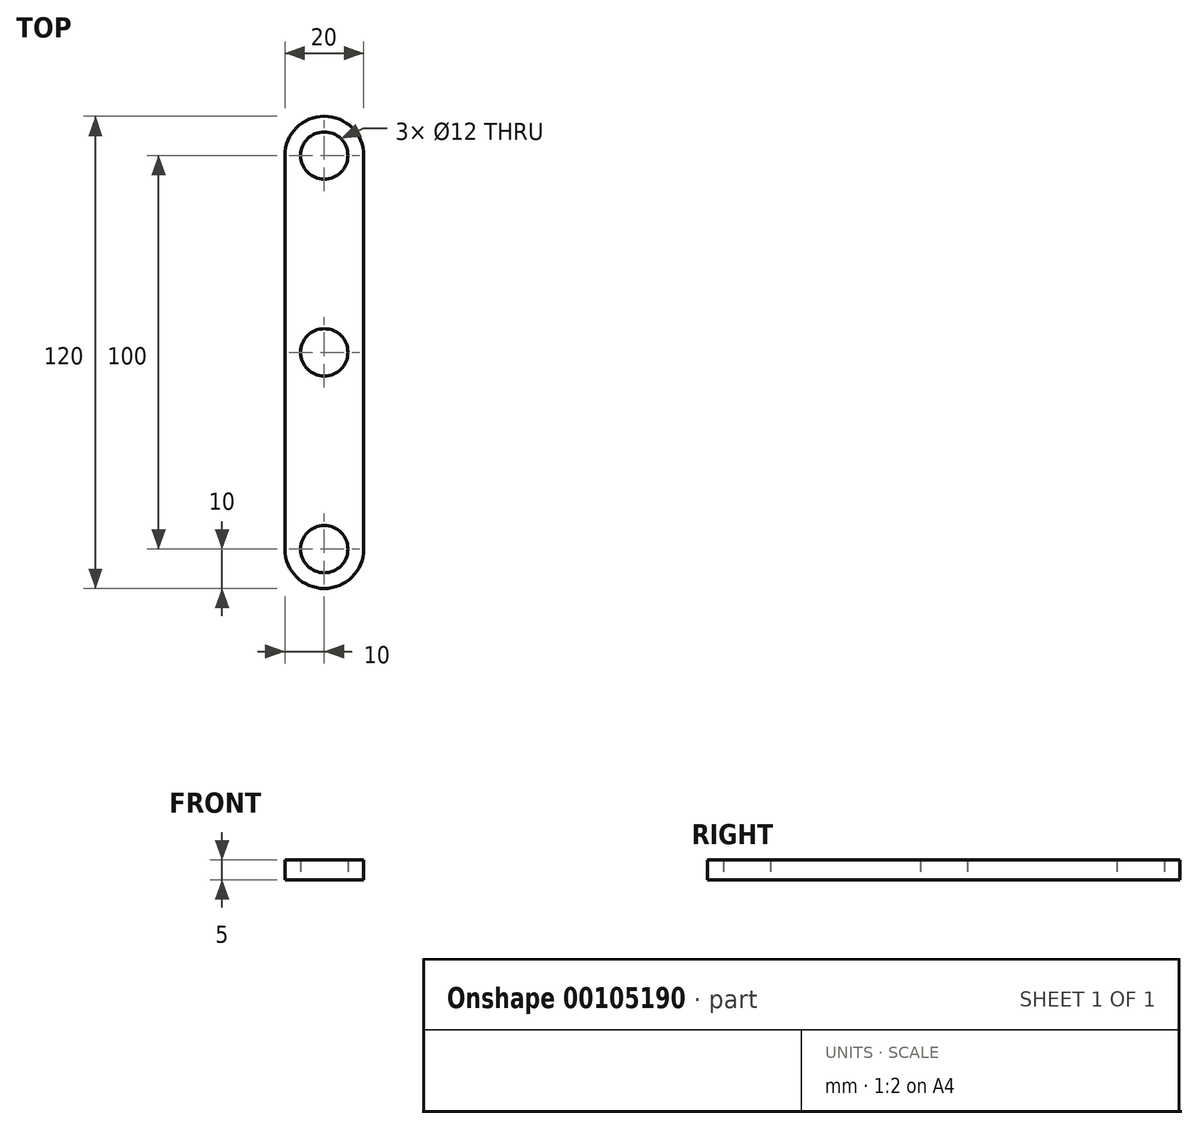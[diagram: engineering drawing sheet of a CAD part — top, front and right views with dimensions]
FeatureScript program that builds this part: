
annotation { "Feature Type Name" : "Feature", "Feature Type Description" : "" }
export const myFeature = defineFeature(function(context is Context, id is Id, definition is map)
    precondition{}
    {
        {
            var Q0;
            Q0=qCreatedBy(makeId("Top.planeOp"),FACE);
            var sketch = newSketch(context, id + "F0", { "sketchPlane" : qUnion([Q0])});
            skCircle(sketch, "E0", {"center": v(0, 0) * mm, "radius": 6 * mm});
            skCircle(sketch, "E1", {"center": v(0, 50) * mm, "radius": 6 * mm});
            skArc(sketch, "E2.0", {"start": v(-10, 0) * mm, "mid": v(0, -10) * mm, "end": v(10, 0) * mm});
            skArc(sketch, "E3", {"start": v(10, 100) * mm, "mid": v(0, 110) * mm, "end": v(-10, 100) * mm});
            skCircle(sketch, "E4", {"center": v(0, 100) * mm, "radius": 6 * mm});
            skLineSegment(sketch, "E5", {"start": v(-10, 100) * mm, "end": v(-10, 0) * mm});
            skLineSegment(sketch, "E6", {"start": v(10, 100) * mm, "end": v(10, 0) * mm});
            skSolve(sketch);
        }
        {
            var Q0;
            Q0=makeQuery(id+"F0.imprint","IMPRINT",FACE,{"disambiguationData":[TD([[makeQuery(id+"F0.imprint","IMPRINT",EDGE,{"derivedFrom":sQuery(id+"F0.wireOp",EDGE,"E0")}),-1.0]])]});
            extrude(context, id + "F1", {"entities" : qUnion([Q0]), "depth" : 5 * mm});
        }
    });
